# Revit family: 204_ff6dc27fab7c4e9d907ed8712ea3d6
name_source: partatom
category: Duct Accessories
units: mm (PartAtom-declared; Revit-internal decimal feet)

## family parameters
Always vertical = Yes
Cut with Voids When Loaded = No
Part Type = Damper
Round Connector Dimension = Use Diameter
Shared = No
Work Plane-Based = No

## types (72) — shared parameters
BBVIS = No
CAT = No
CAT0 = Yes
Description = Fire Damper
ENBL350 = No
FL = 30 mm  [stored 0.0984252 ft]
FL1 = 41 mm  [stored 0.134514 ft]
FLL = 5 mm  [stored 0.0164042 ft]
FLL__ve = -5 mm  [stored -0.0164042 ft]
FW1 = 49 mm  [stored 0.160761 ft]
L = 375 mm
L1 = 130 mm  [stored 0.426509 ft]
L2 = 25 mm  [stored 0.082021 ft]
L2D = 375 mm
L2_2 = 13 mm
L3 = 110 mm  [stored 0.360892 ft]
LLDAndHLD = Yes
LLDONLY = Yes
L_2 = 188 mm
MB = 125 mm  [stored 0.410105 ft]
MC CosPhi = 1
MC Enable LOD 200 = No
MC Enable LOD 350 = No
MC Material1 MAIN_MODEL = MC_0_0_0_0_50
MC Material10 MAIN_MODEL = MC_166_124_83_0_50
MC Material2 MAIN_MODEL = MC_191_191_191_60_50
MC Material3 MAIN_MODEL = MC_191_191_191_0_50
MC Material4 MAIN_MODEL = MC_210_210_210_0_50
MC Material6 MAIN_MODEL = MC_255_255_255_0_50
MC Material7 MAIN_MODEL = MC_255_128_0_0_50
MC Material8 MAIN_MODEL = MC_255_255_255_0_50
MC Number of Poles = 1
MC Voltage = 230 V
MH = 53 mm  [stored 0.173885 ft]
MH1 = 160 mm  [stored 0.524934 ft]
MH1_2 = 80 mm  [stored 0.262467 ft]
MH2 = 140 mm  [stored 0.459318 ft]
MH__ve = -53 mm  [stored -0.173885 ft]
Manufacturer = Mandik
R1 = 72 mm  [stored 0.23622 ft]
R2 = 15 mm  [stored 0.0492126 ft]
R3 = 10 mm  [stored 0.0328084 ft]
URL = https://www.mandik.cz
VIS0 = No
magiPartTypeId = 204
magiProductFamilyId = ff6dc27fab7c4e9d907ed8712ea3d6
zero-valued in all types: Default Elevation

## per-type parameters (varying)
| type | AV | B | B1 | B1_2 | B_2 | CB | CH | CV | H | H1 | H2D | H_2 | MC Active Power | MC Apparent Power | W2D | magiProductId |
| FDMA-180x1000-.40 | Yes | 180 mm | 170 mm  [stored 0.557743 ft] | 85 mm  [stored 0.278871 ft] | 90 mm  [stored 0.295276 ft] | 180 mm  [stored 0.590551 ft] | 1000 mm | Yes | 1000 mm | 990 mm | 1000 mm | 500 mm | 5 W | 5 VA | 180 mm  [stored 0.590551 ft] | 63c00f66e8e3438fa4595c9836deff |
| FDMA-1600x900-.40 | Yes | 1600 mm | 1590 mm | 795 mm | 800 mm | 1600 mm | 900 mm | Yes | 900 mm | 890 mm | 900 mm | 450 mm | 8 W | 8 VA | 1600 mm | f12bcb93ad814a4baecc5535413cab |
| FDMA-1600x800-.40 | Yes | 1600 mm | 1590 mm | 795 mm | 800 mm | 1600 mm | 800 mm | Yes | 800 mm | 790 mm | 800 mm | 400 mm | 8 W | 8 VA | 1600 mm | b8f7813dbd114ade8aaeb19d894e02 |
| FDMA-1600x750-.40 | Yes | 1600 mm | 1590 mm | 795 mm | 800 mm | 1600 mm | 750 mm | Yes | 750 mm | 740 mm | 750 mm | 375 mm | 8 W | 8 VA | 1600 mm | 8e0b087c9f6945719400d65a04cc99 |
| FDMA-1600x710-.40 | Yes | 1600 mm | 1590 mm | 795 mm | 800 mm | 1600 mm | 710 mm | Yes | 710 mm | 700 mm | 710 mm | 355 mm | 8 W | 8 VA | 1600 mm | 9b04c43f3c5f4f75807e877f159fa5 |
| FDMA-1600x700-.40 | Yes | 1600 mm | 1590 mm | 795 mm | 800 mm | 1600 mm | 700 mm | Yes | 700 mm | 690 mm | 700 mm | 350 mm | 8 W | 8 VA | 1600 mm | 45c6fc844d134bf190b987094856a8 |
| FDMA-1600x650-.40 | Yes | 1600 mm | 1590 mm | 795 mm | 800 mm | 1600 mm | 650 mm | Yes | 650 mm | 640 mm | 650 mm | 325 mm | 8 W | 8 VA | 1600 mm | 4235ad0c3e574fb4a293ff9d1a833d |
| FDMA-1600x630-.40 | Yes | 1600 mm | 1590 mm | 795 mm | 800 mm | 1600 mm | 630 mm | Yes | 630 mm | 620 mm | 630 mm | 315 mm | 8 W | 8 VA | 1600 mm | a90cc8682ef54a3abb9390a091e475 |
| FDMA-1600x600-.40 | Yes | 1600 mm | 1590 mm | 795 mm | 800 mm | 1600 mm | 600 mm | Yes | 600 mm | 590 mm | 600 mm | 300 mm | 8 W | 8 VA | 1600 mm | f0c666cfe91c4d4b9e3b795ab6a051 |
| FDMA-1600x560-.40 | Yes | 1600 mm | 1590 mm | 795 mm | 800 mm | 1600 mm | 560 mm | Yes | 560 mm | 550 mm | 560 mm | 280 mm | 8 W | 8 VA | 1600 mm | af33f8237f054095b97db698d5a589 |
| FDMA-1600x550-.40 | Yes | 1600 mm | 1590 mm | 795 mm | 800 mm | 1600 mm | 550 mm | Yes | 550 mm | 540 mm | 550 mm | 275 mm | 8 W | 8 VA | 1600 mm | b13365a2c8ab4bf69ea423c0a242f4 |
| FDMA-1600x500-.40 | No | 1600 mm | 1590 mm | 795 mm | 800 mm | 1600 mm | 500 mm | Yes | 500 mm | 490 mm | 500 mm | 250 mm | 8 W | 8 VA | 1600 mm | e9600d6e4fab44349d06c1dc342c47 |
| FDMA-1600x450-.40 | No | 1600 mm | 1590 mm | 795 mm | 800 mm | 1600 mm | 450 mm | Yes | 450 mm | 440 mm | 450 mm | 225 mm | 8 W | 8 VA | 1600 mm | 172ec3590a9c45d083b23c7ab387e4 |
| FDMA-1600x400-.40 | No | 1600 mm | 1590 mm | 795 mm | 800 mm | 1600 mm | 400 mm | Yes | 400 mm | 390 mm | 400 mm | 200 mm  [stored 0.656168 ft] | 8 W | 8 VA | 1600 mm | 84d1c756282f4751ad296042f1fbc9 |
| FDMA-1600x355-.40 | No | 1600 mm | 1590 mm | 795 mm | 800 mm | 1600 mm | 355 mm | Yes | 355 mm | 345 mm | 355 mm | 178 mm | 5 W | 5 VA | 1600 mm | a14e8be60f3943739d00c33c5b0445 |
| FDMA-1600x315-.40 | No | 1600 mm | 1590 mm | 795 mm | 800 mm | 1600 mm | 315 mm | Yes | 315 mm | 305 mm | 315 mm | 158 mm | 5 W | 5 VA | 1600 mm | 16c2731694644e00874ea7ed07c807 |
| FDMA-1600x300-.40 | No | 1600 mm | 1590 mm | 795 mm | 800 mm | 1600 mm | 300 mm | Yes | 300 mm | 290 mm | 300 mm | 150 mm  [stored 0.492126 ft] | 5 W | 5 VA | 1600 mm | b8b6b6d0ca2749c2916fd32ca486ff |
| FDMA-1600x280-.40 | No | 1600 mm | 1590 mm | 795 mm | 800 mm | 1600 mm | 280 mm | Yes | 280 mm | 270 mm | 280 mm | 140 mm  [stored 0.459318 ft] | 5 W | 5 VA | 1600 mm | bcd8eef981d5483893866f9e53734f |
| FDMA-1600x250-.40 | No | 1600 mm | 1590 mm | 795 mm | 800 mm | 1600 mm | 250 mm | Yes | 250 mm | 240 mm | 250 mm | 125 mm  [stored 0.410105 ft] | 5 W | 5 VA | 1600 mm | 8560c2fd909346deb9d014bdadb83e |
| FDMA-1600x225-.40 | No | 1600 mm | 1590 mm | 795 mm | 800 mm | 1600 mm | 225 mm | No | 225 mm | 215 mm | 225 mm | 113 mm | 4 W | 4 VA | 1600 mm | 82171c53411a4af18cde1326ef40d2 |
| FDMA-1600x200-.40 | No | 1600 mm | 1590 mm | 795 mm | 800 mm | 1600 mm | 200 mm  [stored 0.656168 ft] | No | 200 mm | 190 mm  [stored 0.62336 ft] | 200 mm  [stored 0.656168 ft] | 100 mm  [stored 0.328084 ft] | 4 W | 4 VA | 1600 mm | 918b81186a4f46828cd53d508c128e |
| FDMA-1600x180-.40 | No | 1600 mm | 1590 mm | 795 mm | 800 mm | 1600 mm | 180 mm  [stored 0.590551 ft] | No | 180 mm | 170 mm  [stored 0.557743 ft] | 180 mm  [stored 0.590551 ft] | 90 mm  [stored 0.295276 ft] | 4 W | 4 VA | 1600 mm | 49ed215f7e214d3eaf192fbd639471 |
| FDMA-1600x1000-.40 | Yes | 1600 mm | 1590 mm | 795 mm | 800 mm | 1600 mm | 1000 mm | Yes | 1000 mm | 990 mm | 1000 mm | 500 mm | 8 W | 8 VA | 1600 mm | 3e43b5262df34b60afe24376500de0 |
| FDMA-1500x900-.40 | Yes | 1500 mm | 1490 mm | 745 mm | 750 mm | 1500 mm | 900 mm | Yes | 900 mm | 890 mm | 900 mm | 450 mm | 8 W | 8 VA | 1500 mm | ae525047fd9b471baf0f64cd54ee10 |
| FDMA-1500x1000-.40 | Yes | 1500 mm | 1490 mm | 745 mm | 750 mm | 1500 mm | 1000 mm | Yes | 1000 mm | 990 mm | 1000 mm | 500 mm | 8 W | 8 VA | 1500 mm | 8973c1a541c34242a78ef123750ff2 |
| FDMA-1400x900-.40 | Yes | 1400 mm | 1390 mm | 695 mm | 700 mm | 1400 mm | 900 mm | Yes | 900 mm | 890 mm | 900 mm | 450 mm | 8 W | 8 VA | 1400 mm | 89eaeea4e555438a90c45fe54a5604 |
| FDMA-1400x1000-.40 | Yes | 1400 mm | 1390 mm | 695 mm | 700 mm | 1400 mm | 1000 mm | Yes | 1000 mm | 990 mm | 1000 mm | 500 mm | 8 W | 8 VA | 1400 mm | ec08130001a44e7eb2cb3067ad4c80 |
| FDMA-1250x900-.40 | Yes | 1250 mm | 1240 mm | 620 mm | 625 mm | 1250 mm | 900 mm | Yes | 900 mm | 890 mm | 900 mm | 450 mm | 8 W | 8 VA | 1250 mm | 16cfffb96dd34a15bfe31175eda00d |
| FDMA-1250x1000-.40 | Yes | 1250 mm | 1240 mm | 620 mm | 625 mm | 1250 mm | 1000 mm | Yes | 1000 mm | 990 mm | 1000 mm | 500 mm | 8 W | 8 VA | 1250 mm | 67c4f7d0bd2246ae9217e58a91de90 |
| FDMA-1100x900-.40 | Yes | 1100 mm | 1090 mm | 545 mm | 550 mm | 1100 mm | 900 mm | Yes | 900 mm | 890 mm | 900 mm | 450 mm | 8 W | 8 VA | 1100 mm | 526e1de5ba044659b257b3412ac8e0 |
| FDMA-1100x1000-.40 | Yes | 1100 mm | 1090 mm | 545 mm | 550 mm | 1100 mm | 1000 mm | Yes | 1000 mm | 990 mm | 1000 mm | 500 mm | 8 W | 8 VA | 1100 mm | 95af3351686c42f69daebab81c56aa |
| FDMA-1000x900-.40 | Yes | 1000 mm | 990 mm | 495 mm | 500 mm | 1000 mm | 900 mm | Yes | 900 mm | 890 mm | 900 mm | 450 mm | 8 W | 8 VA | 1000 mm | 2b7862c3e01d4ef2bf730de14f6eab |
| FDMA-1000x1000-.40 | Yes | 1000 mm | 990 mm | 495 mm | 500 mm | 1000 mm | 1000 mm | Yes | 1000 mm | 990 mm | 1000 mm | 500 mm | 8 W | 8 VA | 1000 mm | ec3fdef9a5784630b7d491e60e36b9 |
| FDMA-900x900-.40 | Yes | 900 mm | 890 mm | 445 mm | 450 mm | 900 mm | 900 mm | Yes | 900 mm | 890 mm | 900 mm | 450 mm | 8 W | 8 VA | 900 mm | 0ba3d2cd318743aeb19877ae08c2c7 |
| FDMA-900x1000-.40 | Yes | 900 mm | 890 mm | 445 mm | 450 mm | 900 mm | 1000 mm | Yes | 1000 mm | 990 mm | 1000 mm | 500 mm | 8 W | 8 VA | 900 mm | cc4496d8e61c4e1db3f1dd44fbc323 |
| FDMA-800x900-.40 | Yes | 800 mm | 790 mm | 395 mm | 400 mm | 800 mm | 900 mm | Yes | 900 mm | 890 mm | 900 mm | 450 mm | 8 W | 8 VA | 800 mm | 37212b06a35d4e2e8bd92fc0a316d2 |
| FDMA-800x1000-.40 | Yes | 800 mm | 790 mm | 395 mm | 400 mm | 800 mm | 1000 mm | Yes | 1000 mm | 990 mm | 1000 mm | 500 mm | 8 W | 8 VA | 800 mm | ce18d9f5aedd48e3a85a2bb527bd63 |
| FDMA-750x900-.40 | Yes | 750 mm | 740 mm | 370 mm | 375 mm | 750 mm | 900 mm | Yes | 900 mm | 890 mm | 900 mm | 450 mm | 8 W | 8 VA | 750 mm | 0a5d1fae36b14db2912572142d3f4f |
| FDMA-750x1000-.40 | Yes | 750 mm | 740 mm | 370 mm | 375 mm | 750 mm | 1000 mm | Yes | 1000 mm | 990 mm | 1000 mm | 500 mm | 8 W | 8 VA | 750 mm | d32f734d5dfb49428c5d8f12736931 |
| FDMA-710x900-.40 | Yes | 710 mm | 700 mm | 350 mm | 355 mm | 710 mm | 900 mm | Yes | 900 mm | 890 mm | 900 mm | 450 mm | 8 W | 8 VA | 710 mm | cfe24768ff0845a487673946325010 |
| FDMA-710x1000-.40 | Yes | 710 mm | 700 mm | 350 mm | 355 mm | 710 mm | 1000 mm | Yes | 1000 mm | 990 mm | 1000 mm | 500 mm | 8 W | 8 VA | 710 mm | e4633de17f5347a9a7dbf18f084169 |
| FDMA-700x900-.40 | Yes | 700 mm | 690 mm | 345 mm | 350 mm | 700 mm | 900 mm | Yes | 900 mm | 890 mm | 900 mm | 450 mm | 8 W | 8 VA | 700 mm | 134bc6822cdf48bba7b0921921410b |
| FDMA-700x1000-.40 | Yes | 700 mm | 690 mm | 345 mm | 350 mm | 700 mm | 1000 mm | Yes | 1000 mm | 990 mm | 1000 mm | 500 mm | 8 W | 8 VA | 700 mm | dfebf2157ed249699ad802d202c787 |
| FDMA-650x900-.40 | Yes | 650 mm | 640 mm | 320 mm | 325 mm | 650 mm | 900 mm | Yes | 900 mm | 890 mm | 900 mm | 450 mm | 8 W | 8 VA | 650 mm | 3943000664224a7794fd4c3d774ea4 |
| FDMA-650x1000-.40 | Yes | 650 mm | 640 mm | 320 mm | 325 mm | 650 mm | 1000 mm | Yes | 1000 mm | 990 mm | 1000 mm | 500 mm | 8 W | 8 VA | 650 mm | 0f39ca2c01c449a1872f0caf7548d5 |
| FDMA-630x900-.40 | Yes | 630 mm | 620 mm | 310 mm | 315 mm | 630 mm | 900 mm | Yes | 900 mm | 890 mm | 900 mm | 450 mm | 8 W | 8 VA | 630 mm | ecbece4093c24b6b87835433385e0b |
| FDMA-630x1000-.40 | Yes | 630 mm | 620 mm | 310 mm | 315 mm | 630 mm | 1000 mm | Yes | 1000 mm | 990 mm | 1000 mm | 500 mm | 8 W | 8 VA | 630 mm | 4e433d9bfbc04f73ac843d6c1af5e7 |
| FDMA-600x900-.40 | Yes | 600 mm | 590 mm | 295 mm | 300 mm | 600 mm | 900 mm | Yes | 900 mm | 890 mm | 900 mm | 450 mm | 8 W | 8 VA | 600 mm | a362c675d7c04a508a404713c78324 |
| FDMA-600x1000-.40 | Yes | 600 mm | 590 mm | 295 mm | 300 mm | 600 mm | 1000 mm | Yes | 1000 mm | 990 mm | 1000 mm | 500 mm | 8 W | 8 VA | 600 mm | efafaf6fdcc64e6cbb5804fc0fcef2 |
| FDMA-560x900-.40 | Yes | 560 mm | 550 mm | 275 mm | 280 mm | 560 mm | 900 mm | Yes | 900 mm | 890 mm | 900 mm | 450 mm | 8 W | 8 VA | 560 mm | df207afce2314a73b38a89c09c29b3 |
| FDMA-560x1000-.40 | Yes | 560 mm | 550 mm | 275 mm | 280 mm | 560 mm | 1000 mm | Yes | 1000 mm | 990 mm | 1000 mm | 500 mm | 8 W | 8 VA | 560 mm | e0b76627d683492099eca16aef759c |
| FDMA-550x900-.40 | Yes | 550 mm | 540 mm | 270 mm | 275 mm | 550 mm | 900 mm | Yes | 900 mm | 890 mm | 900 mm | 450 mm | 8 W | 8 VA | 550 mm | 29487ec6343d4d9c9d7cad3d30e34d |
| FDMA-550x1000-.40 | Yes | 550 mm | 540 mm | 270 mm | 275 mm | 550 mm | 1000 mm | Yes | 1000 mm | 990 mm | 1000 mm | 500 mm | 8 W | 8 VA | 550 mm | a00ef0b8a37c464ca532417040df4f |
| FDMA-500x900-.40 | Yes | 500 mm | 490 mm | 245 mm | 250 mm | 500 mm | 900 mm | Yes | 900 mm | 890 mm | 900 mm | 450 mm | 8 W | 8 VA | 500 mm | 3c9058e2280149d6a045b19063332e |
| FDMA-500x1000-.40 | Yes | 500 mm | 490 mm | 245 mm | 250 mm | 500 mm | 1000 mm | Yes | 1000 mm | 990 mm | 1000 mm | 500 mm | 8 W | 8 VA | 500 mm | 708d691578cb403d998a95a5260c8f |
| FDMA-450x900-.40 | Yes | 450 mm | 440 mm | 220 mm  [stored 0.721785 ft] | 225 mm | 450 mm | 900 mm | Yes | 900 mm | 890 mm | 900 mm | 450 mm | 8 W | 8 VA | 450 mm | d6403e3d4334493b85c11887f16dd9 |
| FDMA-450x1000-.40 | Yes | 450 mm | 440 mm | 220 mm  [stored 0.721785 ft] | 225 mm | 450 mm | 1000 mm | Yes | 1000 mm | 990 mm | 1000 mm | 500 mm | 8 W | 8 VA | 450 mm | d0e07485a6ab4adb8f8d2fd5af2011 |
| FDMA-400x900-.40 | Yes | 400 mm | 390 mm | 195 mm  [stored 0.639764 ft] | 200 mm  [stored 0.656168 ft] | 400 mm | 900 mm | Yes | 900 mm | 890 mm | 900 mm | 450 mm | 8 W | 8 VA | 400 mm | eaaa0cf899dc46d5ae67979821453f |
| FDMA-400x1000-.40 | Yes | 400 mm | 390 mm | 195 mm  [stored 0.639764 ft] | 200 mm  [stored 0.656168 ft] | 400 mm | 1000 mm | Yes | 1000 mm | 990 mm | 1000 mm | 500 mm | 8 W | 8 VA | 400 mm | 80f4ae03fedf41c590ec6ba3fa1562 |
| FDMA-355x900-.40 | Yes | 355 mm | 345 mm | 173 mm  [stored 0.567585 ft] | 178 mm | 355 mm | 900 mm | Yes | 900 mm | 890 mm | 900 mm | 450 mm | 8 W | 8 VA | 355 mm | eeb2d5f414214853bbfdc06058021c |
| FDMA-355x1000-.40 | Yes | 355 mm | 345 mm | 173 mm  [stored 0.567585 ft] | 178 mm | 355 mm | 1000 mm | Yes | 1000 mm | 990 mm | 1000 mm | 500 mm | 8 W | 8 VA | 355 mm | 83a011408f5f43c9ad5498ba86dd20 |
| FDMA-315x900-.40 | Yes | 315 mm | 305 mm | 153 mm | 158 mm | 315 mm | 900 mm | Yes | 900 mm | 890 mm | 900 mm | 450 mm | 8 W | 8 VA | 315 mm | fc1d84010e2947b2a795754027f07f |
| FDMA-315x1000-.40 | Yes | 315 mm | 305 mm | 153 mm | 158 mm | 315 mm | 1000 mm | Yes | 1000 mm | 990 mm | 1000 mm | 500 mm | 8 W | 8 VA | 315 mm | 9c5558dadd464affbb1f7acaa1ff9a |
| FDMA-300x900-.40 | Yes | 300 mm | 290 mm | 145 mm  [stored 0.475722 ft] | 150 mm  [stored 0.492126 ft] | 300 mm | 900 mm | Yes | 900 mm | 890 mm | 900 mm | 450 mm | 8 W | 8 VA | 300 mm | 7fca17876ee64f3ba2fcaaad9bbb53 |
| FDMA-300x1000-.40 | Yes | 300 mm | 290 mm | 145 mm  [stored 0.475722 ft] | 150 mm  [stored 0.492126 ft] | 300 mm | 1000 mm | Yes | 1000 mm | 990 mm | 1000 mm | 500 mm | 8 W | 8 VA | 300 mm | 82db4b7015c8412692e24e645e387f |
| FDMA-280x900-.40 | Yes | 280 mm | 270 mm | 135 mm  [stored 0.442913 ft] | 140 mm  [stored 0.459318 ft] | 280 mm | 900 mm | Yes | 900 mm | 890 mm | 900 mm | 450 mm | 8 W | 8 VA | 280 mm | bbf4626d26dc42f8912c35a7b3aad2 |
| FDMA-280x1000-.40 | Yes | 280 mm | 270 mm | 135 mm  [stored 0.442913 ft] | 140 mm  [stored 0.459318 ft] | 280 mm | 1000 mm | Yes | 1000 mm | 990 mm | 1000 mm | 500 mm | 8 W | 8 VA | 280 mm | dc9e81e405674497b50756beea8c1e |
| FDMA-250x900-.40 | Yes | 250 mm | 240 mm | 120 mm  [stored 0.393701 ft] | 125 mm  [stored 0.410105 ft] | 250 mm | 900 mm | Yes | 900 mm | 890 mm | 900 mm | 450 mm | 5 W | 5 VA | 250 mm | 72c8d028254f434aa2f40702f53ffd |
| FDMA-250x1000-.40 | Yes | 250 mm | 240 mm | 120 mm  [stored 0.393701 ft] | 125 mm  [stored 0.410105 ft] | 250 mm | 1000 mm | Yes | 1000 mm | 990 mm | 1000 mm | 500 mm | 8 W | 8 VA | 250 mm | 2fa52ab6748c428a8a49e3e229e9da |
| FDMA-200x900-.40 | Yes | 200 mm | 190 mm  [stored 0.62336 ft] | 95 mm  [stored 0.31168 ft] | 100 mm  [stored 0.328084 ft] | 200 mm  [stored 0.656168 ft] | 900 mm | Yes | 900 mm | 890 mm | 900 mm | 450 mm | 5 W | 5 VA | 200 mm  [stored 0.656168 ft] | 5882b9024e284f24a750583ef53e25 |
| FDMA-200x1000-.40 | Yes | 200 mm | 190 mm  [stored 0.62336 ft] | 95 mm  [stored 0.31168 ft] | 100 mm  [stored 0.328084 ft] | 200 mm  [stored 0.656168 ft] | 1000 mm | Yes | 1000 mm | 990 mm | 1000 mm | 500 mm | 5 W | 5 VA | 200 mm  [stored 0.656168 ft] | 4324b91ccfec42749e7214142f10bc |
| FDMA-180x900-.40 | Yes | 180 mm | 170 mm  [stored 0.557743 ft] | 85 mm  [stored 0.278871 ft] | 90 mm  [stored 0.295276 ft] | 180 mm  [stored 0.590551 ft] | 900 mm | Yes | 900 mm | 890 mm | 900 mm | 450 mm | 5 W | 5 VA | 180 mm  [stored 0.590551 ft] | 01597ad167f348f7a745269575a0d4 |

note: column(s) folded — value = type name in every type: MC Product Code

note: [stored X ft] marks values corroborated as IEEE doubles in the binary element streams (Revit-internal decimal feet)

## geometry (parser evidence)
native form markers: Sweep x7
no freeform markers — native parametric forms only
